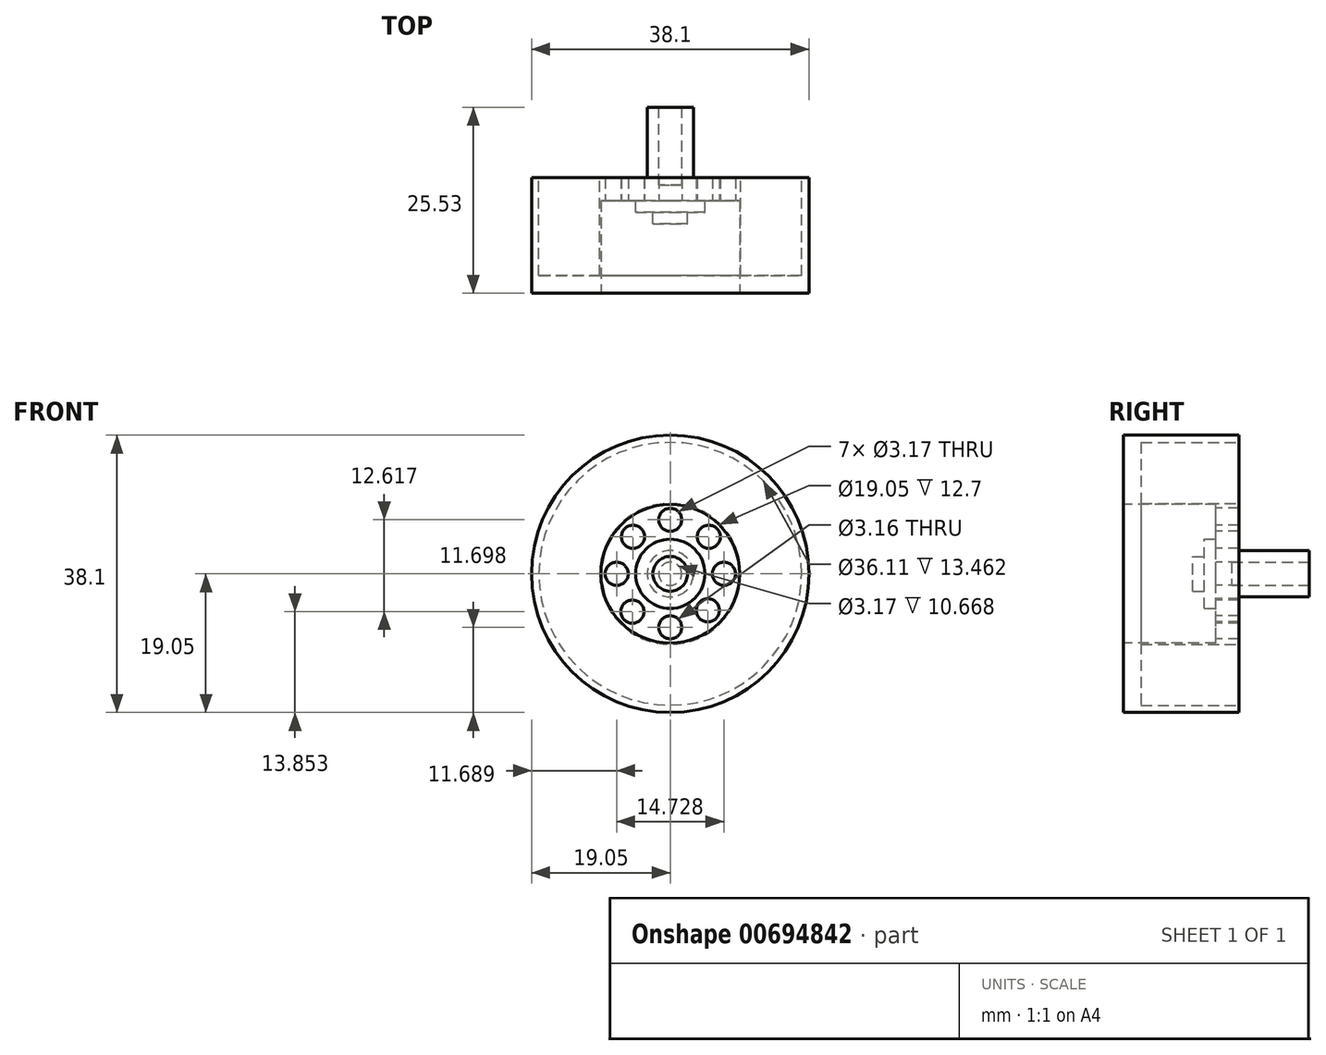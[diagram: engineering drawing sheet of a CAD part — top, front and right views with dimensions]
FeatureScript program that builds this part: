
annotation { "Feature Type Name" : "Feature", "Feature Type Description" : "" }
export const myFeature = defineFeature(function(context is Context, id is Id, definition is map)
    precondition{}
    {
        {
            var Q0;
            Q0=qCreatedBy(makeId("Front.planeOp"),FACE);
            var sketch = newSketch(context, id + "F0", { "sketchPlane" : qUnion([Q0])});
            skCircle(sketch, "E0", {"center": v(0, 0) * mm, "radius": 19.05 * mm});
            skSolve(sketch);
        }
        {
            var Q0;
            Q0 = qSketchRegion(id + "F0", true);
            extrude(context, id + "F1", {"entities" : qUnion([Q0]), "oppositeDirection" : true, "depth" : 15.88 * mm, "offsetDistance" : 25.4 * mm});
        }
        {
            var Q0;
            Q0=makeQuery(id+"F1.opExtrude","CAP_FACE",FACE,{"disambiguationData":[OSD([sQuery(id+"F0.wireOp",EDGE,"E0")])],"isStart":true});
            var sketch = newSketch(context, id + "F2", { "sketchPlane" : qUnion([Q0])});
            skCircle(sketch, "E1", {"center": v(0, 0) * mm, "radius": 9.53 * mm});
            skSolve(sketch);
        }
        {
            var Q0;
            Q0 = qSketchRegion(id + "F2", true);
            extrude(context, id + "F3", {"entities" : qUnion([Q0]), "operationType" : NewBodyOperationType.REMOVE, "oppositeDirection" : true, "depth" : 12.7 * mm, "offsetDistance" : 25.4 * mm});
        }
        {
            var Q0;
            Q0=makeQuery(id+"F3.boolean.opBoolean","COPY",FACE,{"derivedFrom":makeQuery(id+"F3.opExtrude","CAP_FACE",FACE,{"disambiguationData":[OSD([sQuery(id+"F2.wireOp",EDGE,"E1")])],"isStart":false})});
            var sketch = newSketch(context, id + "F4", { "sketchPlane" : qUnion([Q0])});
            skSolve(sketch);
        }
        {
            var Q0;
            Q0=makeQuery(id+"F4.imprint","IMPRINT",FACE,{"disambiguationData":[TD([[makeQuery(id+"F4.imprint","IMPRINT",EDGE,{"derivedFrom":makeQuery(id+"F3.boolean.opBoolean","COPY",EDGE,{"derivedFrom":makeQuery(id+"F3.opExtrude","CAP_EDGE",EDGE,{"disambiguationData":[OSD([sQuery(id+"F2.wireOp",EDGE,"E1")])],"isStart":false})})}),1.0]])]});
            var sketch = newSketch(context, id + "F5", { "sketchPlane" : qUnion([Q0])});
            skCircle(sketch, "E2", {"center": v(0, 7.42) * mm, "radius": 1.59 * mm});
            skSolve(sketch);
        }
        {
            var Q0;
            Q0 = qSketchRegion(id + "F5", true);
            extrude(context, id + "F6", {"entities" : qUnion([Q0]), "operationType" : NewBodyOperationType.REMOVE, "oppositeDirection" : true, "depth" : 25.4 * mm, "offsetDistance" : 25.4 * mm});
        }
        {
            var Q0;
            Q0=makeQuery(id+"F4.imprint","IMPRINT",FACE,{"disambiguationData":[TD([[makeQuery(id+"F4.imprint","IMPRINT",EDGE,{"derivedFrom":makeQuery(id+"F3.boolean.opBoolean","COPY",EDGE,{"derivedFrom":makeQuery(id+"F3.opExtrude","CAP_EDGE",EDGE,{"disambiguationData":[OSD([sQuery(id+"F2.wireOp",EDGE,"E1")])],"isStart":false})})}),1.0]])]});
            var sketch = newSketch(context, id + "F7", { "sketchPlane" : qUnion([Q0])});
            skCircle(sketch, "E3", {"center": v(0, -7.35) * mm, "radius": 1.58 * mm});
            skSolve(sketch);
        }
        {
            var Q0;
            Q0 = qSketchRegion(id + "F7", true);
            extrude(context, id + "F8", {"entities" : qUnion([Q0]), "operationType" : NewBodyOperationType.REMOVE, "oppositeDirection" : true, "depth" : 25.4 * mm, "offsetDistance" : 25.4 * mm});
        }
        {
            var Q0;
            Q0=makeQuery(id+"F4.imprint","IMPRINT",FACE,{"disambiguationData":[TD([[makeQuery(id+"F4.imprint","IMPRINT",EDGE,{"derivedFrom":makeQuery(id+"F3.boolean.opBoolean","COPY",EDGE,{"derivedFrom":makeQuery(id+"F3.opExtrude","CAP_EDGE",EDGE,{"disambiguationData":[OSD([sQuery(id+"F2.wireOp",EDGE,"E1")])],"isStart":false})})}),1.0]])]});
            var sketch = newSketch(context, id + "F9", { "sketchPlane" : qUnion([Q0])});
            skCircle(sketch, "E4", {"center": v(-7.36, 0) * mm, "radius": 1.59 * mm});
            skSolve(sketch);
        }
        {
            var Q0;
            Q0 = qSketchRegion(id + "F9", true);
            extrude(context, id + "F10", {"entities" : qUnion([Q0]), "operationType" : NewBodyOperationType.REMOVE, "oppositeDirection" : true, "depth" : 25.4 * mm, "offsetDistance" : 25.4 * mm});
        }
        {
            var Q0;
            Q0=makeQuery(id+"F4.imprint","IMPRINT",FACE,{"disambiguationData":[TD([[makeQuery(id+"F4.imprint","IMPRINT",EDGE,{"derivedFrom":makeQuery(id+"F3.boolean.opBoolean","COPY",EDGE,{"derivedFrom":makeQuery(id+"F3.opExtrude","CAP_EDGE",EDGE,{"disambiguationData":[OSD([sQuery(id+"F2.wireOp",EDGE,"E1")])],"isStart":false})})}),1.0]])]});
            var sketch = newSketch(context, id + "F11", { "sketchPlane" : qUnion([Q0])});
            skCircle(sketch, "E5", {"center": v(7.37, 0) * mm, "radius": 1.59 * mm});
            skSolve(sketch);
        }
        {
            var Q0;
            Q0 = qSketchRegion(id + "F11", true);
            extrude(context, id + "F12", {"entities" : qUnion([Q0]), "operationType" : NewBodyOperationType.REMOVE, "oppositeDirection" : true, "depth" : 25.4 * mm, "offsetDistance" : 25.4 * mm});
        }
        {
            var Q0;
            Q0=makeQuery(id+"F4.imprint","IMPRINT",FACE,{"disambiguationData":[TD([[makeQuery(id+"F4.imprint","IMPRINT",EDGE,{"derivedFrom":makeQuery(id+"F3.boolean.opBoolean","COPY",EDGE,{"derivedFrom":makeQuery(id+"F3.opExtrude","CAP_EDGE",EDGE,{"disambiguationData":[OSD([sQuery(id+"F2.wireOp",EDGE,"E1")])],"isStart":false})})}),1.0]])]});
            var sketch = newSketch(context, id + "F13", { "sketchPlane" : qUnion([Q0])});
            skCircle(sketch, "E6", {"center": v(-5.12, 5.09) * mm, "radius": 1.59 * mm});
            skSolve(sketch);
        }
        {
            var Q0;
            Q0 = qSketchRegion(id + "F13", true);
            extrude(context, id + "F14", {"entities" : qUnion([Q0]), "operationType" : NewBodyOperationType.REMOVE, "oppositeDirection" : true, "depth" : 25.4 * mm, "offsetDistance" : 25.4 * mm});
        }
        {
            var Q0;
            Q0=makeQuery(id+"F4.imprint","IMPRINT",FACE,{"disambiguationData":[TD([[makeQuery(id+"F4.imprint","IMPRINT",EDGE,{"derivedFrom":makeQuery(id+"F3.boolean.opBoolean","COPY",EDGE,{"derivedFrom":makeQuery(id+"F3.opExtrude","CAP_EDGE",EDGE,{"disambiguationData":[OSD([sQuery(id+"F2.wireOp",EDGE,"E1")])],"isStart":false})})}),1.0]])]});
            var sketch = newSketch(context, id + "F15", { "sketchPlane" : qUnion([Q0])});
            skCircle(sketch, "E7", {"center": v(5.3, 5.09) * mm, "radius": 1.59 * mm});
            skSolve(sketch);
        }
        {
            var Q0;
            Q0 = qSketchRegion(id + "F15", true);
            extrude(context, id + "F16", {"entities" : qUnion([Q0]), "operationType" : NewBodyOperationType.REMOVE, "oppositeDirection" : true, "depth" : 25.4 * mm, "offsetDistance" : 25.4 * mm});
        }
        {
            var Q0;
            Q0=makeQuery(id+"F4.imprint","IMPRINT",FACE,{"disambiguationData":[TD([[makeQuery(id+"F4.imprint","IMPRINT",EDGE,{"derivedFrom":makeQuery(id+"F3.boolean.opBoolean","COPY",EDGE,{"derivedFrom":makeQuery(id+"F3.opExtrude","CAP_EDGE",EDGE,{"disambiguationData":[OSD([sQuery(id+"F2.wireOp",EDGE,"E1")])],"isStart":false})})}),1.0]])]});
            var sketch = newSketch(context, id + "F17", { "sketchPlane" : qUnion([Q0])});
            skCircle(sketch, "E8", {"center": v(-5.2, -5.2) * mm, "radius": 1.59 * mm});
            skSolve(sketch);
        }
        {
            var Q0;
            Q0 = qSketchRegion(id + "F17", true);
            extrude(context, id + "F18", {"entities" : qUnion([Q0]), "operationType" : NewBodyOperationType.REMOVE, "oppositeDirection" : true, "depth" : 25.4 * mm, "offsetDistance" : 25.4 * mm});
        }
        {
            var Q0;
            Q0=makeQuery(id+"F4.imprint","IMPRINT",FACE,{"disambiguationData":[TD([[makeQuery(id+"F4.imprint","IMPRINT",EDGE,{"derivedFrom":makeQuery(id+"F3.boolean.opBoolean","COPY",EDGE,{"derivedFrom":makeQuery(id+"F3.opExtrude","CAP_EDGE",EDGE,{"disambiguationData":[OSD([sQuery(id+"F2.wireOp",EDGE,"E1")])],"isStart":false})})}),1.0]])]});
            var sketch = newSketch(context, id + "F19", { "sketchPlane" : qUnion([Q0])});
            skCircle(sketch, "E9", {"center": v(5.17, -5.02) * mm, "radius": 1.59 * mm});
            skSolve(sketch);
        }
        {
            var Q0;
            Q0 = qSketchRegion(id + "F19", true);
            extrude(context, id + "F20", {"entities" : qUnion([Q0]), "operationType" : NewBodyOperationType.REMOVE, "oppositeDirection" : true, "depth" : 25.4 * mm, "offsetDistance" : 25.4 * mm});
        }
        {
            var Q0;
            Q0=makeQuery(id+"F4.imprint","IMPRINT",FACE,{"disambiguationData":[TD([[makeQuery(id+"F4.imprint","IMPRINT",EDGE,{"derivedFrom":makeQuery(id+"F3.boolean.opBoolean","COPY",EDGE,{"derivedFrom":makeQuery(id+"F3.opExtrude","CAP_EDGE",EDGE,{"disambiguationData":[OSD([sQuery(id+"F2.wireOp",EDGE,"E1")])],"isStart":false})})}),1.0]])]});
            var sketch = newSketch(context, id + "F21", { "sketchPlane" : qUnion([Q0])});
            skCircle(sketch, "E10", {"center": v(0, 0) * mm, "radius": 4.76 * mm});
            skSolve(sketch);
        }
        {
            var Q0;
            Q0 = qSketchRegion(id + "F21", true);
            extrude(context, id + "F22", {"entities" : qUnion([Q0]), "operationType" : NewBodyOperationType.ADD, "depth" : 1.59 * mm, "offsetDistance" : 25.4 * mm});
        }
        {
            var Q0;
            Q0=makeQuery(id+"F22.opExtrude","CAP_FACE",FACE,{"disambiguationData":[OSD([sQuery(id+"F21.wireOp",EDGE,"E10")])],"isStart":false});
            var sketch = newSketch(context, id + "F23", { "sketchPlane" : qUnion([Q0])});
            skCircle(sketch, "E11", {"center": v(0, 0) * mm, "radius": 2.38 * mm});
            skSolve(sketch);
        }
        {
            var Q0;
            Q0 = qSketchRegion(id + "F23", true);
            extrude(context, id + "F24", {"entities" : qUnion([Q0]), "operationType" : NewBodyOperationType.ADD, "depth" : 1.59 * mm, "offsetDistance" : 25.4 * mm});
        }
        {
            var Q0;
            Q0=makeQuery(id+"F1.opExtrude","CAP_FACE",FACE,{"disambiguationData":[OSD([sQuery(id+"F0.wireOp",EDGE,"E0")])],"isStart":false});
            var sketch = newSketch(context, id + "F25", { "sketchPlane" : qUnion([Q0])});
            skCircle(sketch, "E12", {"center": v(0, 0) * mm, "radius": 18.05 * mm});
            skSolve(sketch);
        }
        {
            var Q0;
            Q0=makeQuery(id+"F25.imprint","IMPRINT",FACE,{"disambiguationData":[TD([[makeQuery(id+"F25.imprint","IMPRINT",EDGE,{"derivedFrom":sQuery(id+"F25.wireOp",EDGE,"E12")}),1.0]])]});
            var sketch = newSketch(context, id + "F26", { "sketchPlane" : qUnion([Q0])});
            skCircle(sketch, "E13", {"center": v(0, 0) * mm, "radius": 9.68 * mm});
            skCircle(sketch, "E14.0", {"center": v(0, 0) * mm, "radius": 18.05 * mm});
            skSolve(sketch);
        }
        {
            var Q0;
            Q0=makeQuery(id+"F26.imprint","IMPRINT",FACE,{"disambiguationData":[TD([[makeQuery(id+"F26.imprint","IMPRINT",EDGE,{"derivedFrom":sQuery(id+"F26.wireOp",EDGE,"E13")}),-1.0]])]});
            extrude(context, id + "F27", {"entities" : qUnion([Q0]), "operationType" : NewBodyOperationType.REMOVE, "oppositeDirection" : true, "depth" : 13.46 * mm, "offsetDistance" : 25.4 * mm});
        }
        {
            var Q0;
            Q0=makeQuery(id+"F25.imprint","IMPRINT",FACE,{"disambiguationData":[TD([[makeQuery(id+"F25.imprint","IMPRINT",EDGE,{"derivedFrom":sQuery(id+"F25.wireOp",EDGE,"E12")}),1.0]])]});
            var sketch = newSketch(context, id + "F28", { "sketchPlane" : qUnion([Q0])});
            skCircle(sketch, "E15", {"center": v(0, 0) * mm, "radius": 3.18 * mm});
            skSolve(sketch);
        }
        {
            var Q0;
            Q0 = qSketchRegion(id + "F28", true);
            extrude(context, id + "F29", {"entities" : qUnion([Q0]), "operationType" : NewBodyOperationType.ADD, "depth" : 9.65 * mm, "offsetDistance" : 25.4 * mm});
        }
        {
            var Q0;
            Q0=makeQuery(id+"F29.opExtrude","CAP_FACE",FACE,{"disambiguationData":[OSD([sQuery(id+"F28.wireOp",EDGE,"E15")])],"isStart":false});
            var sketch = newSketch(context, id + "F30", { "sketchPlane" : qUnion([Q0])});
            skCircle(sketch, "E16", {"center": v(0, 0) * mm, "radius": 1.59 * mm});
            skSolve(sketch);
        }
        {
            var Q0;
            Q0 = qSketchRegion(id + "F30", true);
            extrude(context, id + "F31", {"entities" : qUnion([Q0]), "operationType" : NewBodyOperationType.REMOVE, "oppositeDirection" : true, "depth" : 10.67 * mm, "offsetDistance" : 25.4 * mm});
        }
    });
